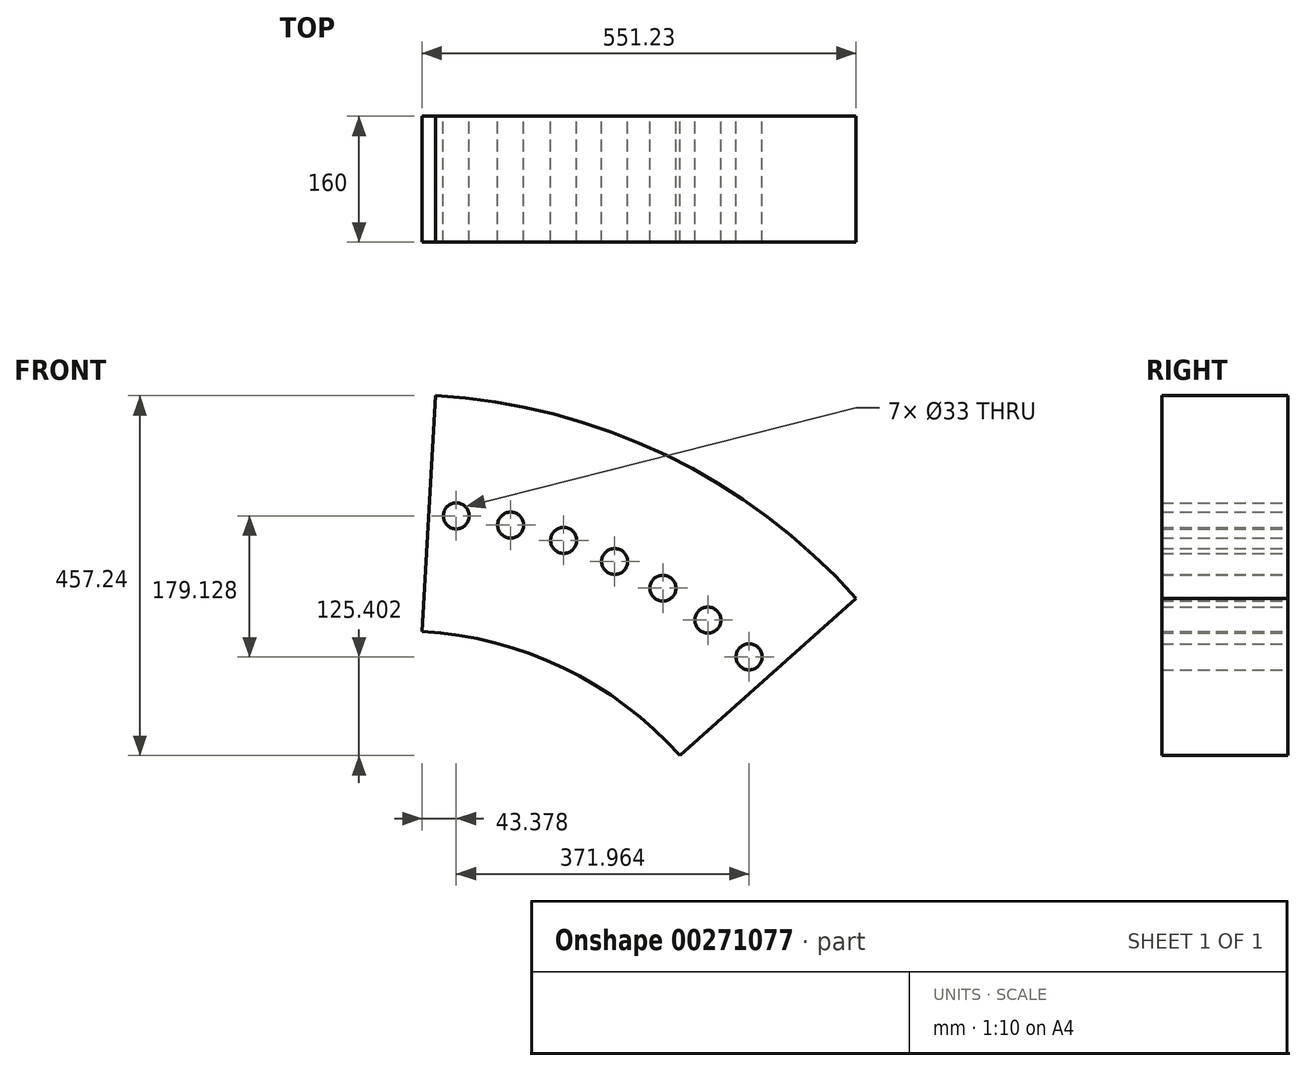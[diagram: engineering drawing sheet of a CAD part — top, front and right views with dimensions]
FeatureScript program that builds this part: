
annotation { "Feature Type Name" : "Feature", "Feature Type Description" : "" }
export const myFeature = defineFeature(function(context is Context, id is Id, definition is map)
    precondition{}
    {
        {
            var Q0;
            Q0=qCreatedBy(makeId("Front.planeOp"),FACE);
            var sketch = newSketch(context, id + "F0", { "sketchPlane" : qUnion([Q0])});
            skCircle(sketch, "E0", {"center": v(0, 625) * mm, "radius": 16.5 * mm});
            skCircle(sketch, "E1.1.0", {"center": v(-69.98, 621.07) * mm, "radius": 16.5 * mm});
            skCircle(sketch, "E1.2.0", {"center": v(-139.08, 609.33) * mm, "radius": 16.5 * mm});
            skCircle(sketch, "E1.3.0", {"center": v(-206.42, 589.93) * mm, "radius": 16.5 * mm});
            skCircle(sketch, "E1.4.0", {"center": v(-271.18, 563.1) * mm, "radius": 16.5 * mm});
            skCircle(sketch, "E1.5.0", {"center": v(-332.52, 529.2) * mm, "radius": 16.5 * mm});
            skCircle(sketch, "E1.6.0", {"center": v(-389.68, 488.64) * mm, "radius": 16.5 * mm});
            skCircle(sketch, "E1.7.0", {"center": v(-441.94, 441.94) * mm, "radius": 16.5 * mm});
            skCircle(sketch, "E1.8.0", {"center": v(-488.64, 389.68) * mm, "radius": 16.5 * mm});
            skCircle(sketch, "E1.9.0", {"center": v(-529.2, 332.52) * mm, "radius": 16.5 * mm});
            skCircle(sketch, "E1.10.0", {"center": v(-563.1, 271.18) * mm, "radius": 16.5 * mm});
            skCircle(sketch, "E1.11.0", {"center": v(-589.93, 206.42) * mm, "radius": 16.5 * mm});
            skCircle(sketch, "E1.12.0", {"center": v(-609.33, 139.08) * mm, "radius": 16.5 * mm});
            skCircle(sketch, "E1.13.0", {"center": v(-621.07, 69.98) * mm, "radius": 16.5 * mm});
            skCircle(sketch, "E1.14.0", {"center": v(-625, 0) * mm, "radius": 16.5 * mm});
            skCircle(sketch, "E1.15.0", {"center": v(-621.07, -69.98) * mm, "radius": 16.5 * mm});
            skCircle(sketch, "E1.16.0", {"center": v(-609.33, -139.08) * mm, "radius": 16.5 * mm});
            skCircle(sketch, "E1.17.0", {"center": v(-589.93, -206.42) * mm, "radius": 16.5 * mm});
            skCircle(sketch, "E1.18.0", {"center": v(-563.1, -271.18) * mm, "radius": 16.5 * mm});
            skCircle(sketch, "E1.19.0", {"center": v(-529.2, -332.52) * mm, "radius": 16.5 * mm});
            skCircle(sketch, "E1.20.0", {"center": v(-488.64, -389.68) * mm, "radius": 16.5 * mm});
            skCircle(sketch, "E1.21.0", {"center": v(-441.94, -441.94) * mm, "radius": 16.5 * mm});
            skCircle(sketch, "E1.22.0", {"center": v(-389.68, -488.64) * mm, "radius": 16.5 * mm});
            skCircle(sketch, "E1.23.0", {"center": v(-332.52, -529.2) * mm, "radius": 16.5 * mm});
            skCircle(sketch, "E1.24.0", {"center": v(-271.18, -563.1) * mm, "radius": 16.5 * mm});
            skCircle(sketch, "E1.25.0", {"center": v(-206.42, -589.93) * mm, "radius": 16.5 * mm});
            skCircle(sketch, "E1.26.0", {"center": v(-139.08, -609.33) * mm, "radius": 16.5 * mm});
            skCircle(sketch, "E1.27.0", {"center": v(-69.98, -621.07) * mm, "radius": 16.5 * mm});
            skCircle(sketch, "E1.28.0", {"center": v(0, -625) * mm, "radius": 16.5 * mm});
            skCircle(sketch, "E1.29.0", {"center": v(69.98, -621.07) * mm, "radius": 16.5 * mm});
            skCircle(sketch, "E1.30.0", {"center": v(139.08, -609.33) * mm, "radius": 16.5 * mm});
            skCircle(sketch, "E1.31.0", {"center": v(206.42, -589.93) * mm, "radius": 16.5 * mm});
            skCircle(sketch, "E1.32.0", {"center": v(271.18, -563.1) * mm, "radius": 16.5 * mm});
            skCircle(sketch, "E1.33.0", {"center": v(332.52, -529.2) * mm, "radius": 16.5 * mm});
            skCircle(sketch, "E1.34.0", {"center": v(389.68, -488.64) * mm, "radius": 16.5 * mm});
            skCircle(sketch, "E1.35.0", {"center": v(441.94, -441.94) * mm, "radius": 16.5 * mm});
            skCircle(sketch, "E1.36.0", {"center": v(488.64, -389.68) * mm, "radius": 16.5 * mm});
            skCircle(sketch, "E1.37.0", {"center": v(529.2, -332.52) * mm, "radius": 16.5 * mm});
            skCircle(sketch, "E1.38.0", {"center": v(563.1, -271.18) * mm, "radius": 16.5 * mm});
            skCircle(sketch, "E1.39.0", {"center": v(589.93, -206.42) * mm, "radius": 16.5 * mm});
            skCircle(sketch, "E1.40.0", {"center": v(609.33, -139.08) * mm, "radius": 16.5 * mm});
            skCircle(sketch, "E1.41.0", {"center": v(621.07, -69.98) * mm, "radius": 16.5 * mm});
            skCircle(sketch, "E1.42.0", {"center": v(625, 0) * mm, "radius": 16.5 * mm});
            skCircle(sketch, "E1.43.0", {"center": v(621.07, 69.98) * mm, "radius": 16.5 * mm});
            skCircle(sketch, "E1.44.0", {"center": v(609.33, 139.08) * mm, "radius": 16.5 * mm});
            skCircle(sketch, "E1.45.0", {"center": v(589.93, 206.42) * mm, "radius": 16.5 * mm});
            skCircle(sketch, "E1.46.0", {"center": v(563.1, 271.18) * mm, "radius": 16.5 * mm});
            skCircle(sketch, "E1.47.0", {"center": v(529.2, 332.52) * mm, "radius": 16.5 * mm});
            skCircle(sketch, "E1.48.0", {"center": v(488.64, 389.68) * mm, "radius": 16.5 * mm});
            skCircle(sketch, "E1.49.0", {"center": v(441.94, 441.94) * mm, "radius": 16.5 * mm});
            skCircle(sketch, "E1.50.0", {"center": v(389.68, 488.64) * mm, "radius": 16.5 * mm});
            skCircle(sketch, "E1.51.0", {"center": v(332.52, 529.2) * mm, "radius": 16.5 * mm});
            skCircle(sketch, "E1.52.0", {"center": v(271.18, 563.1) * mm, "radius": 16.5 * mm});
            skCircle(sketch, "E1.53.0", {"center": v(206.42, 589.93) * mm, "radius": 16.5 * mm});
            skCircle(sketch, "E1.54.0", {"center": v(139.08, 609.33) * mm, "radius": 16.5 * mm});
            skCircle(sketch, "E1.55.0", {"center": v(69.98, 621.07) * mm, "radius": 16.5 * mm});
            skPoint(sketch, "E1.center", {"position": v(0, 0) * mm});
            skLineSegment(sketch, "E1.anchor1", {"start": v(0, 0) * mm, "end": v(0, 625) * mm, "construction": true});
            skLineSegment(sketch, "E1.anchor2", {"start": v(0, 0) * mm, "end": v(69.98, 621.07) * mm, "construction": true});
            skCircle(sketch, "E2", {"center": v(0, 0) * mm, "radius": 475 * mm});
            skCircle(sketch, "E3", {"center": v(0, 0) * mm, "radius": 775 * mm});
            skSolve(sketch);
        }
        {
            var Q0;
            Q0=makeQuery(id+"F0.imprint","IMPRINT",FACE,{"disambiguationData":[TD([[makeQuery(id+"F0.imprint","IMPRINT",EDGE,{"derivedFrom":sQuery(id+"F0.wireOp",EDGE,"E0")}),-1.0]])]});
            extrude(context, id + "F1", {"entities" : qUnion([Q0]), "depth" : 160 * mm});
        }
        {
            var Q0;
            Q0=qCreatedBy(makeId("Front.planeOp"),FACE);
            var sketch = newSketch(context, id + "F2", { "sketchPlane" : qUnion([Q0])});
            skLineSegment(sketch, "E4", {"start": v(0, 0) * mm, "end": v(78.17, 1393.82) * mm});
            skLineSegment(sketch, "E5", {"start": v(0, 0) * mm, "end": v(1136.47, 1015.76) * mm});
            skLineSegment(sketch, "E6", {"start": v(78.17, 1393.82) * mm, "end": v(1136.47, 1015.76) * mm});
            skSolve(sketch);
        }
        {
            var Q0;
            Q0=makeQuery(id+"F2.imprint","IMPRINT",FACE,{"disambiguationData":[TD([[makeQuery(id+"F2.imprint","IMPRINT",EDGE,{"derivedFrom":sQuery(id+"F2.wireOp",EDGE,"E4")}),-1.0]])]});
            extrude(context, id + "F3", {"entities" : qUnion([Q0]), "depth" : 160 * mm});
        }
        {
            var Q0;
            Q0=makeQuery(id+"F1.opExtrude","SWEPT_BODY",BODY,{"disambiguationData":[OSD([sQuery(id+"F0.wireOp",EDGE,"E0"),sQuery(id+"F0.wireOp",EDGE,"E1.1.0"),sQuery(id+"F0.wireOp",EDGE,"E1.2.0"),sQuery(id+"F0.wireOp",EDGE,"E1.3.0"),sQuery(id+"F0.wireOp",EDGE,"E1.4.0"),sQuery(id+"F0.wireOp",EDGE,"E1.5.0"),sQuery(id+"F0.wireOp",EDGE,"E1.6.0"),sQuery(id+"F0.wireOp",EDGE,"E1.7.0"),sQuery(id+"F0.wireOp",EDGE,"E1.8.0"),sQuery(id+"F0.wireOp",EDGE,"E1.9.0"),sQuery(id+"F0.wireOp",EDGE,"E1.10.0"),sQuery(id+"F0.wireOp",EDGE,"E1.11.0"),sQuery(id+"F0.wireOp",EDGE,"E1.12.0"),sQuery(id+"F0.wireOp",EDGE,"E1.13.0"),sQuery(id+"F0.wireOp",EDGE,"E1.14.0"),sQuery(id+"F0.wireOp",EDGE,"E1.15.0"),sQuery(id+"F0.wireOp",EDGE,"E1.16.0"),sQuery(id+"F0.wireOp",EDGE,"E1.17.0"),sQuery(id+"F0.wireOp",EDGE,"E1.18.0"),sQuery(id+"F0.wireOp",EDGE,"E1.19.0"),sQuery(id+"F0.wireOp",EDGE,"E1.20.0"),sQuery(id+"F0.wireOp",EDGE,"E1.21.0"),sQuery(id+"F0.wireOp",EDGE,"E1.22.0"),sQuery(id+"F0.wireOp",EDGE,"E1.23.0"),sQuery(id+"F0.wireOp",EDGE,"E1.24.0"),sQuery(id+"F0.wireOp",EDGE,"E1.25.0"),sQuery(id+"F0.wireOp",EDGE,"E1.26.0"),sQuery(id+"F0.wireOp",EDGE,"E1.27.0"),sQuery(id+"F0.wireOp",EDGE,"E1.28.0"),sQuery(id+"F0.wireOp",EDGE,"E1.29.0"),sQuery(id+"F0.wireOp",EDGE,"E1.30.0"),sQuery(id+"F0.wireOp",EDGE,"E1.31.0"),sQuery(id+"F0.wireOp",EDGE,"E1.32.0"),sQuery(id+"F0.wireOp",EDGE,"E1.33.0"),sQuery(id+"F0.wireOp",EDGE,"E1.34.0"),sQuery(id+"F0.wireOp",EDGE,"E1.35.0"),sQuery(id+"F0.wireOp",EDGE,"E1.36.0"),sQuery(id+"F0.wireOp",EDGE,"E1.37.0"),sQuery(id+"F0.wireOp",EDGE,"E1.38.0"),sQuery(id+"F0.wireOp",EDGE,"E1.39.0"),sQuery(id+"F0.wireOp",EDGE,"E1.40.0"),sQuery(id+"F0.wireOp",EDGE,"E1.41.0"),sQuery(id+"F0.wireOp",EDGE,"E1.42.0"),sQuery(id+"F0.wireOp",EDGE,"E1.43.0"),sQuery(id+"F0.wireOp",EDGE,"E1.44.0"),sQuery(id+"F0.wireOp",EDGE,"E1.45.0"),sQuery(id+"F0.wireOp",EDGE,"E1.46.0"),sQuery(id+"F0.wireOp",EDGE,"E1.47.0"),sQuery(id+"F0.wireOp",EDGE,"E1.48.0"),sQuery(id+"F0.wireOp",EDGE,"E1.49.0"),sQuery(id+"F0.wireOp",EDGE,"E1.50.0"),sQuery(id+"F0.wireOp",EDGE,"E1.51.0"),sQuery(id+"F0.wireOp",EDGE,"E1.52.0"),sQuery(id+"F0.wireOp",EDGE,"E1.53.0"),sQuery(id+"F0.wireOp",EDGE,"E1.54.0"),sQuery(id+"F0.wireOp",EDGE,"E1.55.0"),sQuery(id+"F0.wireOp",EDGE,"E2"),sQuery(id+"F0.wireOp",EDGE,"E3")])]});
            var Q1;
            Q1=makeQuery(id+"F3.opExtrude","SWEPT_BODY",BODY,{"disambiguationData":[OSD([sQuery(id+"F2.wireOp",EDGE,"E4"),sQuery(id+"F2.wireOp",EDGE,"E5"),sQuery(id+"F2.wireOp",EDGE,"E6")])]});
            booleanBodies(context, id + "F4", {"operationType" : BooleanOperationType.INTERSECTION, "tools" : qUnion([Q0, Q1])});
        }
    });
